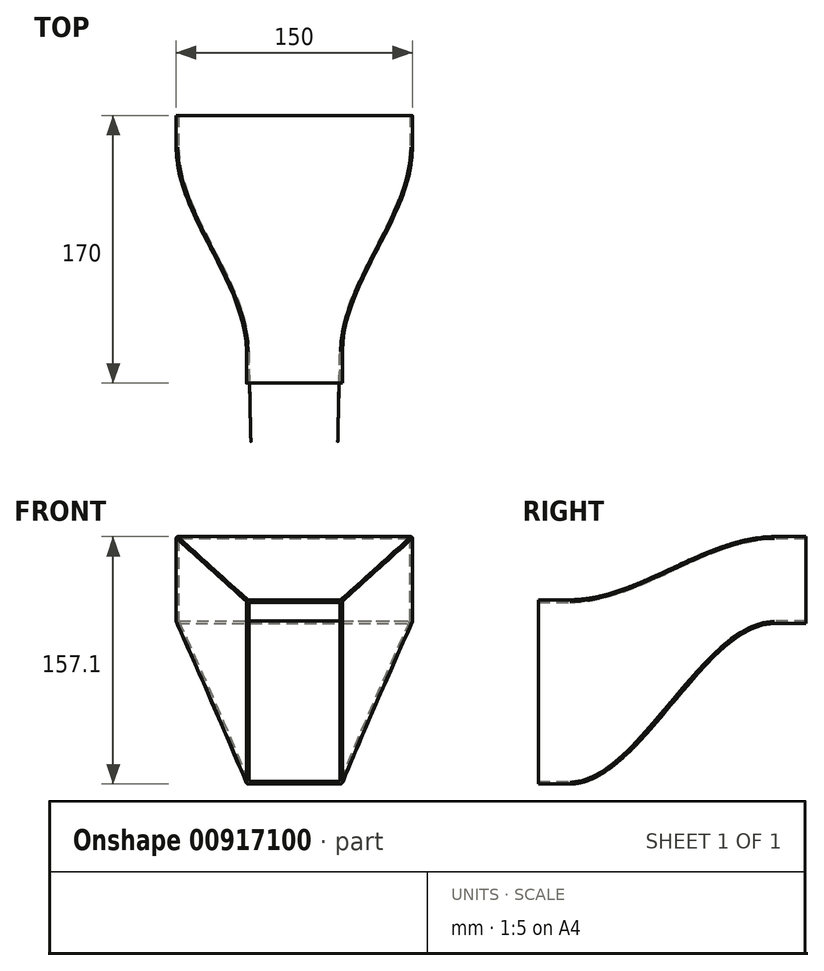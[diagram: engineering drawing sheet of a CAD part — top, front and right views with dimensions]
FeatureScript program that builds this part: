
annotation { "Feature Type Name" : "Feature", "Feature Type Description" : "" }
export const myFeature = defineFeature(function(context is Context, id is Id, definition is map)
    precondition{}
    {
        {
            var Q0;
            Q0=qCreatedBy(makeId("Front.planeOp"),FACE);
            var sketch = newSketch(context, id + "F0", { "sketchPlane" : qUnion([Q0])});
            skLineSegment(sketch, "E0.bottom", {"start": v(-75.1, 55.1) * mm, "end": v(74.9, 55.1) * mm});
            skLineSegment(sketch, "E0.top", {"start": v(-75.1, 0.1) * mm, "end": v(74.9, 0.1) * mm});
            skLineSegment(sketch, "E0.left", {"start": v(-75.1, 55.1) * mm, "end": v(-75.1, 0.1) * mm});
            skLineSegment(sketch, "E0.right", {"start": v(74.9, 55.1) * mm, "end": v(74.9, 0.1) * mm});
            skSolve(sketch);
        }
        {
            var Q0;
            Q0=qCreatedBy(makeId("Front.planeOp"),FACE);
            var Q1;
            Q1 = qBodyType(qCreatedBy(id + "F2" ,EDGE), BodyType.WIRE);
            cPlane(context, id + "F1", {"entities" : qUnion([Q0, Q1]), "cplaneType" : CPlaneType.OFFSET, "offset" : 130 * mm, "width" : 150 * mm, "height" : 150 * mm});
        }
        {
            var Q0;
            Q0=qCreatedBy(id+"F1.planeOp",FACE);
            var sketch = newSketch(context, id + "F2", { "sketchPlane" : qUnion([Q0])});
            skLineSegment(sketch, "E1.bottom", {"start": v(-30.6, 15) * mm, "end": v(30.4, 15) * mm});
            skLineSegment(sketch, "E1.top", {"start": v(-30.6, -102) * mm, "end": v(30.4, -102) * mm});
            skLineSegment(sketch, "E1.left", {"start": v(-30.6, 15) * mm, "end": v(-30.6, -102) * mm});
            skLineSegment(sketch, "E1.right", {"start": v(30.4, 15) * mm, "end": v(30.4, -102) * mm});
            skSolve(sketch);
        }
        {
            var Q0;
            Q0=makeQuery(id+"F0.imprint","IMPRINT",FACE,{"disambiguationData":[TD([[makeQuery(id+"F0.imprint","IMPRINT",EDGE,{"derivedFrom":sQuery(id+"F0.wireOp",EDGE,"E0.bottom")}),-1.0]])]});
            var Q1;
            Q1=makeQuery(id+"F2.imprint","IMPRINT",FACE,{"disambiguationData":[TD([[makeQuery(id+"F2.imprint","IMPRINT",EDGE,{"derivedFrom":sQuery(id+"F2.wireOp",EDGE,"E1.bottom")}),-1.0]])]});
            loft(context, id + "F3", {"startCondition" : LoftEndDerivativeType.NORMAL_TO_PROFILE, "startMagnitude" : 1, "endCondition" : LoftEndDerivativeType.NORMAL_TO_PROFILE, "endMagnitude" : 1, "sheetProfilesArray" : [{ "sheetProfileEntities" : qUnion([Q0]) }, { "sheetProfileEntities" : qUnion([Q1]) }]});
        }
        {
            var Q0;
            Q0=makeQuery(id+"F3.opLoft","CAP_FACE",FACE,{"disambiguationData":[OSD([makeQuery(id+"F2.imprint","IMPRINT",FACE,{"disambiguationData":[TD([[makeQuery(id+"F2.imprint","IMPRINT",EDGE,{"derivedFrom":sQuery(id+"F2.wireOp",EDGE,"E1.bottom")}),-1.0]])]})])],"isStart":true});
            extrude(context, id + "F4", {"entities" : qUnion([Q0]), "operationType" : NewBodyOperationType.ADD, "depth" : 20 * mm, "offsetDistance" : 25 * mm});
        }
        {
            var Q0;
            Q0=makeQuery(id+"F3.opLoft","CAP_FACE",FACE,{"disambiguationData":[OSD([makeQuery(id+"F0.imprint","IMPRINT",FACE,{"disambiguationData":[TD([[makeQuery(id+"F0.imprint","IMPRINT",EDGE,{"derivedFrom":sQuery(id+"F0.wireOp",EDGE,"E0.bottom")}),-1.0]])]})])],"isStart":true});
            extrude(context, id + "F5", {"entities" : qUnion([Q0]), "operationType" : NewBodyOperationType.ADD, "depth" : 20 * mm, "offsetDistance" : 25 * mm});
        }
        {
            var Q0;
            Q0=makeQuery(id+"F4.opExtrude","CAP_FACE",FACE,{"disambiguationData":[OSD([makeQuery(id+"F2.imprint","IMPRINT",FACE,{"disambiguationData":[TD([[makeQuery(id+"F2.imprint","IMPRINT",EDGE,{"derivedFrom":sQuery(id+"F2.wireOp",EDGE,"E1.bottom")}),-1.0]])]})])],"isStart":false});
            var Q1;
            Q1=makeQuery(id+"F5.opExtrude","CAP_FACE",FACE,{"disambiguationData":[OSD([makeQuery(id+"F0.imprint","IMPRINT",FACE,{"disambiguationData":[TD([[makeQuery(id+"F0.imprint","IMPRINT",EDGE,{"derivedFrom":sQuery(id+"F0.wireOp",EDGE,"E0.bottom")}),-1.0]])]})])],"isStart":false});
            shell(context, id + "F6", {"entities" : qUnion([Q0, Q1]), "thickness" : 1.6 * mm});
        }
        {
            var Q0;
            Q0=makeQuery(id+"F5.opExtrude","SWEPT_EDGE",EDGE,{"disambiguationData":[OSD([sQuery(id+"F0.wireOp",EDGE,"E0.top"),sQuery(id+"F0.wireOp",EDGE,"E0.right")])]});
            var Q1;
            Q1=makeQuery(id+"F5.opExtrude","SWEPT_EDGE",EDGE,{"disambiguationData":[OSD([sQuery(id+"F0.wireOp",EDGE,"E0.top"),sQuery(id+"F0.wireOp",EDGE,"E0.left")])]});
            var Q2;
            Q2=makeQuery(id+"F5.opExtrude","SWEPT_EDGE",EDGE,{"disambiguationData":[OSD([sQuery(id+"F0.wireOp",EDGE,"E0.bottom"),sQuery(id+"F0.wireOp",EDGE,"E0.left")])]});
            var Q3;
            Q3=makeQuery(id+"F5.opExtrude","SWEPT_EDGE",EDGE,{"disambiguationData":[OSD([sQuery(id+"F0.wireOp",EDGE,"E0.bottom"),sQuery(id+"F0.wireOp",EDGE,"E0.right")])]});
            fillet(context, id + "F7", {"entities" : qUnion([Q0, Q1, Q2, Q3]), "radius" : 1 * mm, "tangentPropagation" : true, "allowEdgeOverflow" : false});
        }
    });
